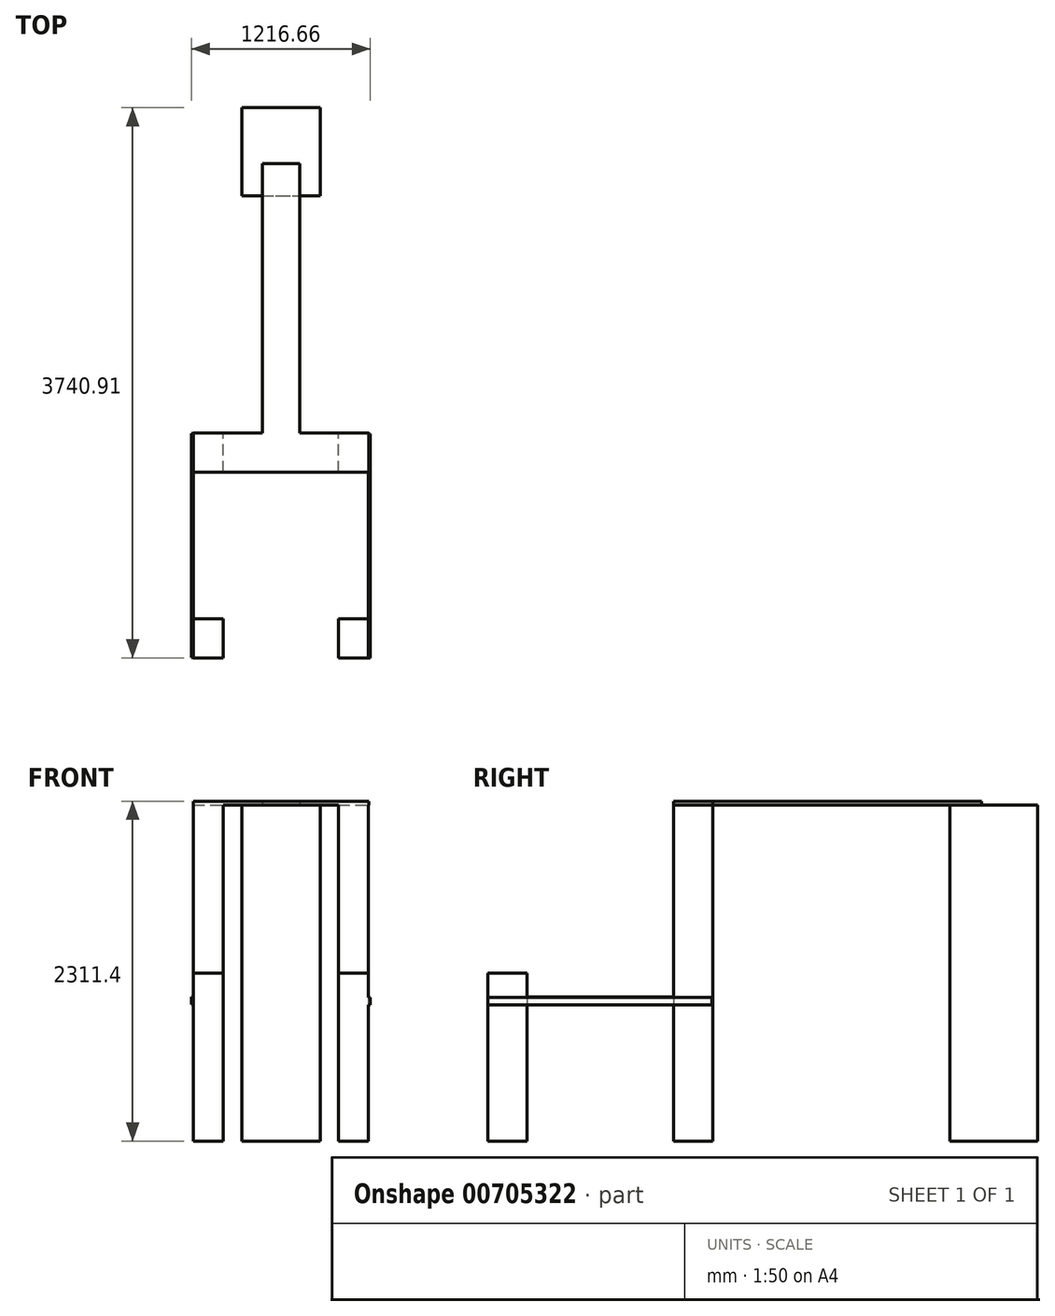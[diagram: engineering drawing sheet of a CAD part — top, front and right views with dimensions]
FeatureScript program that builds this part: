
annotation { "Feature Type Name" : "Feature", "Feature Type Description" : "" }
export const myFeature = defineFeature(function(context is Context, id is Id, definition is map)
    precondition{}
    {
        {
            var Q0;
            Q0=qCreatedBy(makeId("Top.planeOp"),FACE);
            var sketch = newSketch(context, id + "F0", { "sketchPlane" : qUnion([Q0])});
            skLineSegment(sketch, "E0.bottom", {"start": v(0, 0) * mm, "end": v(203.2, 0) * mm});
            skLineSegment(sketch, "E0.top", {"start": v(0, 266.7) * mm, "end": v(203.2, 266.7) * mm});
            skLineSegment(sketch, "E0.left", {"start": v(0, 0) * mm, "end": v(0, 266.7) * mm});
            skLineSegment(sketch, "E0.right", {"start": v(203.2, 0) * mm, "end": v(203.2, 266.7) * mm});
            skLineSegment(sketch, "E1.bottom", {"start": v(988.06, 0) * mm, "end": v(1191.26, 0) * mm});
            skLineSegment(sketch, "E1.top", {"start": v(988.06, 266.7) * mm, "end": v(1191.26, 266.7) * mm});
            skLineSegment(sketch, "E1.left", {"start": v(988.06, 0) * mm, "end": v(988.06, 266.7) * mm});
            skLineSegment(sketch, "E1.right", {"start": v(1191.26, 0) * mm, "end": v(1191.26, 266.7) * mm});
            skLineSegment(sketch, "E2.bottom", {"start": v(0, 1261.87) * mm, "end": v(203.2, 1261.87) * mm});
            skLineSegment(sketch, "E2.top", {"start": v(0, 1528.57) * mm, "end": v(203.2, 1528.57) * mm});
            skLineSegment(sketch, "E2.left", {"start": v(0, 1261.87) * mm, "end": v(0, 1528.57) * mm});
            skLineSegment(sketch, "E2.right", {"start": v(203.2, 1261.87) * mm, "end": v(203.2, 1528.57) * mm});
            skPoint(sketch, "E3", {"position": v(101.6, 1261.87) * mm});
            skLineSegment(sketch, "E4.bottom", {"start": v(988.06, 1261.87) * mm, "end": v(1191.26, 1261.87) * mm});
            skLineSegment(sketch, "E4.top", {"start": v(988.06, 1528.57) * mm, "end": v(1191.26, 1528.57) * mm});
            skLineSegment(sketch, "E4.left", {"start": v(988.06, 1261.87) * mm, "end": v(988.06, 1528.57) * mm});
            skLineSegment(sketch, "E4.right", {"start": v(1191.26, 1261.87) * mm, "end": v(1191.26, 1528.57) * mm});
            skPoint(sketch, "E5", {"position": v(1089.66, 1261.87) * mm});
            skLineSegment(sketch, "E6.bottom", {"start": v(328.93, 3142.74) * mm, "end": v(862.33, 3142.74) * mm});
            skLineSegment(sketch, "E6.top", {"start": v(328.93, 3740.91) * mm, "end": v(862.33, 3740.91) * mm});
            skLineSegment(sketch, "E6.left", {"start": v(328.93, 3142.74) * mm, "end": v(328.93, 3740.91) * mm});
            skLineSegment(sketch, "E6.right", {"start": v(862.33, 3142.74) * mm, "end": v(862.33, 3740.91) * mm});
            skSolve(sketch);
        }
        {
            var Q0;
            Q0=makeQuery(id+"F0.imprint","IMPRINT",FACE,{"disambiguationData":[TD([[makeQuery(id+"F0.imprint","IMPRINT",EDGE,{"derivedFrom":sQuery(id+"F0.wireOp",EDGE,"E6.bottom")}),1.0]])]});
            var Q1;
            Q1=makeQuery(id+"F0.imprint","IMPRINT",FACE,{"disambiguationData":[TD([[makeQuery(id+"F0.imprint","IMPRINT",EDGE,{"derivedFrom":sQuery(id+"F0.wireOp",EDGE,"E4.bottom")}),1.0]])]});
            var Q2;
            Q2=makeQuery(id+"F0.imprint","IMPRINT",FACE,{"disambiguationData":[TD([[makeQuery(id+"F0.imprint","IMPRINT",EDGE,{"derivedFrom":sQuery(id+"F0.wireOp",EDGE,"E2.bottom")}),1.0]])]});
            var Q3;
            Q3=makeQuery(id+"F0.imprint","IMPRINT",FACE,{"disambiguationData":[TD([[makeQuery(id+"F0.imprint","IMPRINT",EDGE,{"derivedFrom":sQuery(id+"F0.wireOp",EDGE,"E0.bottom")}),1.0]])]});
            var Q4;
            Q4=makeQuery(id+"F0.imprint","IMPRINT",FACE,{"disambiguationData":[TD([[makeQuery(id+"F0.imprint","IMPRINT",EDGE,{"derivedFrom":sQuery(id+"F0.wireOp",EDGE,"E1.bottom")}),1.0]])]});
            extrude(context, id + "F1", {"entities" : qUnion([Q0, Q1, Q2, Q3, Q4]), "depth" : 1143 * mm, "offsetDistance" : 25.4 * mm});
        }
        {
            var Q0;
            Q0=makeQuery(id+"F1.opExtrude","CAP_FACE",FACE,{"disambiguationData":[OSD([sQuery(id+"F0.wireOp",EDGE,"E2.bottom"),sQuery(id+"F0.wireOp",EDGE,"E2.top"),sQuery(id+"F0.wireOp",EDGE,"E2.left"),sQuery(id+"F0.wireOp",EDGE,"E2.right")])],"isStart":false});
            var Q1;
            Q1=makeQuery(id+"F1.opExtrude","CAP_FACE",FACE,{"disambiguationData":[OSD([sQuery(id+"F0.wireOp",EDGE,"E4.bottom"),sQuery(id+"F0.wireOp",EDGE,"E4.top"),sQuery(id+"F0.wireOp",EDGE,"E4.left"),sQuery(id+"F0.wireOp",EDGE,"E4.right")])],"isStart":false});
            var Q2;
            Q2=makeQuery(id+"F1.opExtrude","CAP_FACE",FACE,{"disambiguationData":[OSD([sQuery(id+"F0.wireOp",EDGE,"E6.bottom"),sQuery(id+"F0.wireOp",EDGE,"E6.top"),sQuery(id+"F0.wireOp",EDGE,"E6.left"),sQuery(id+"F0.wireOp",EDGE,"E6.right")])],"isStart":false});
            extrude(context, id + "F2", {"entities" : qUnion([Q0, Q1, Q2]), "operationType" : NewBodyOperationType.ADD, "depth" : 1143 * mm, "offsetDistance" : 25.4 * mm});
        }
        {
            var Q0;
            Q0=makeQuery(id+"F2.opExtrude","CAP_FACE",FACE,{"disambiguationData":[OSD([sQuery(id+"F0.wireOp",EDGE,"E2.bottom"),sQuery(id+"F0.wireOp",EDGE,"E2.top"),sQuery(id+"F0.wireOp",EDGE,"E2.left"),sQuery(id+"F0.wireOp",EDGE,"E2.right")])],"isStart":false});
            var sketch = newSketch(context, id + "F3", { "sketchPlane" : qUnion([Q0])});
            skLineSegment(sketch, "E7.bottom", {"start": v(0, 1261.87) * mm, "end": v(1192.86, 1261.87) * mm});
            skLineSegment(sketch, "E7.top", {"start": v(0, 1530.08) * mm, "end": v(471.46, 1530.08) * mm});
            skLineSegment(sketch, "E7.left", {"start": v(0, 1261.87) * mm, "end": v(0, 1530.08) * mm});
            skLineSegment(sketch, "E7.right", {"start": v(1192.86, 1261.87) * mm, "end": v(1192.86, 1530.08) * mm});
            skLineSegment(sketch, "E8.top", {"start": v(471.46, 3360.06) * mm, "end": v(723.08, 3360.06) * mm});
            skLineSegment(sketch, "E8.left", {"start": v(471.46, 1530.08) * mm, "end": v(471.46, 3360.06) * mm});
            skLineSegment(sketch, "E8.right", {"start": v(723.08, 1530.08) * mm, "end": v(723.08, 3360.06) * mm});
            skLineSegment(sketch, "E9.trimOffspring", {"start": v(723.08, 1530.08) * mm, "end": v(1192.86, 1530.08) * mm});
            skSolve(sketch);
        }
        {
            var Q0;
            {var subQ2=sQuery(id+"F3.wireOp",EDGE,"E7.top");Q0=makeQuery(id+"F3.imprint","IMPRINT",FACE,{"disambiguationData":[TD([[makeQuery(id+"F3.imprint","IMPRINT",EDGE,{"derivedFrom":subQ2}),-1.0]])]});}
            var Q1;
            {var subQ4=makeQuery(id+"F2.opExtrude","CAP_EDGE",EDGE,{"disambiguationData":[OSD([sQuery(id+"F0.wireOp",EDGE,"E2.top")])],"isStart":false});Q1=makeQuery(id+"F3.imprint","IMPRINT",FACE,{"disambiguationData":[TD([[makeQuery(id+"F3.imprint","IMPRINT",EDGE,{"derivedFrom":subQ4}),-1.0]])]});}
            extrude(context, id + "F4", {"entities" : qUnion([Q0, Q1]), "operationType" : NewBodyOperationType.ADD, "depth" : 25.4 * mm, "offsetDistance" : 25.4 * mm});
        }
        {
            var Q0;
            Q0=makeQuery(id+"F1.opExtrude","SWEPT_FACE",FACE,{"disambiguationData":[OSD([sQuery(id+"F0.wireOp",EDGE,"E1.right")])]});
            var sketch = newSketch(context, id + "F5", { "sketchPlane" : qUnion([Q0])});
            skLineSegment(sketch, "E10.bottom", {"start": v(0, 975.2) * mm, "end": v(1524, 975.2) * mm});
            skLineSegment(sketch, "E10.top", {"start": v(0, 924.4) * mm, "end": v(1524, 924.4) * mm});
            skLineSegment(sketch, "E10.left", {"start": v(0, 975.2) * mm, "end": v(0, 924.4) * mm});
            skLineSegment(sketch, "E10.right", {"start": v(1524, 975.2) * mm, "end": v(1524, 924.4) * mm});
            skSolve(sketch);
        }
        {
            var Q0;
            Q0=makeQuery(id+"F1.opExtrude","SWEPT_FACE",FACE,{"disambiguationData":[OSD([sQuery(id+"F0.wireOp",EDGE,"E0.left")])]});
            var sketch = newSketch(context, id + "F6", { "sketchPlane" : qUnion([Q0])});
            skLineSegment(sketch, "E11.bottom", {"start": v(-1525, 979.01) * mm, "end": v(-1, 979.01) * mm});
            skLineSegment(sketch, "E11.top", {"start": v(-1525, 928.21) * mm, "end": v(-1, 928.21) * mm});
            skLineSegment(sketch, "E11.left", {"start": v(-1525, 979.01) * mm, "end": v(-1525, 928.21) * mm});
            skLineSegment(sketch, "E11.right", {"start": v(-1, 979.01) * mm, "end": v(-1, 928.21) * mm});
            skSolve(sketch);
        }
        {
            var Q0;
            {var subQ0=sQuery(id+"F6.wireOp",EDGE,"E11.left");Q0=makeQuery(id+"F6.imprint","IMPRINT",FACE,{"disambiguationData":[TD([[makeQuery(id+"F6.imprint","IMPRINT",EDGE,{"derivedFrom":subQ0}),1.0]])]});}
            var Q1;
            {var subQ0=sQuery(id+"F6.wireOp",EDGE,"E11.right");Q1=makeQuery(id+"F6.imprint","IMPRINT",FACE,{"disambiguationData":[TD([[makeQuery(id+"F6.imprint","IMPRINT",EDGE,{"derivedFrom":subQ0}),-1.0]])]});}
            extrude(context, id + "F7", {"entities" : qUnion([Q0, Q1]), "operationType" : NewBodyOperationType.ADD, "depth" : 12.7 * mm, "offsetDistance" : 25.4 * mm});
        }
        {
            var Q0;
            {var subQ0=sQuery(id+"F5.wireOp",EDGE,"E10.right");Q0=makeQuery(id+"F5.imprint","IMPRINT",FACE,{"disambiguationData":[TD([[makeQuery(id+"F5.imprint","IMPRINT",EDGE,{"derivedFrom":subQ0}),-1.0]])]});}
            var Q1;
            {var subQ0=sQuery(id+"F5.wireOp",EDGE,"E10.left");Q1=makeQuery(id+"F5.imprint","IMPRINT",FACE,{"disambiguationData":[TD([[makeQuery(id+"F5.imprint","IMPRINT",EDGE,{"derivedFrom":subQ0}),1.0]])]});}
            extrude(context, id + "F8", {"entities" : qUnion([Q0, Q1]), "operationType" : NewBodyOperationType.ADD, "depth" : 12.7 * mm, "offsetDistance" : 25.4 * mm});
        }
    });
